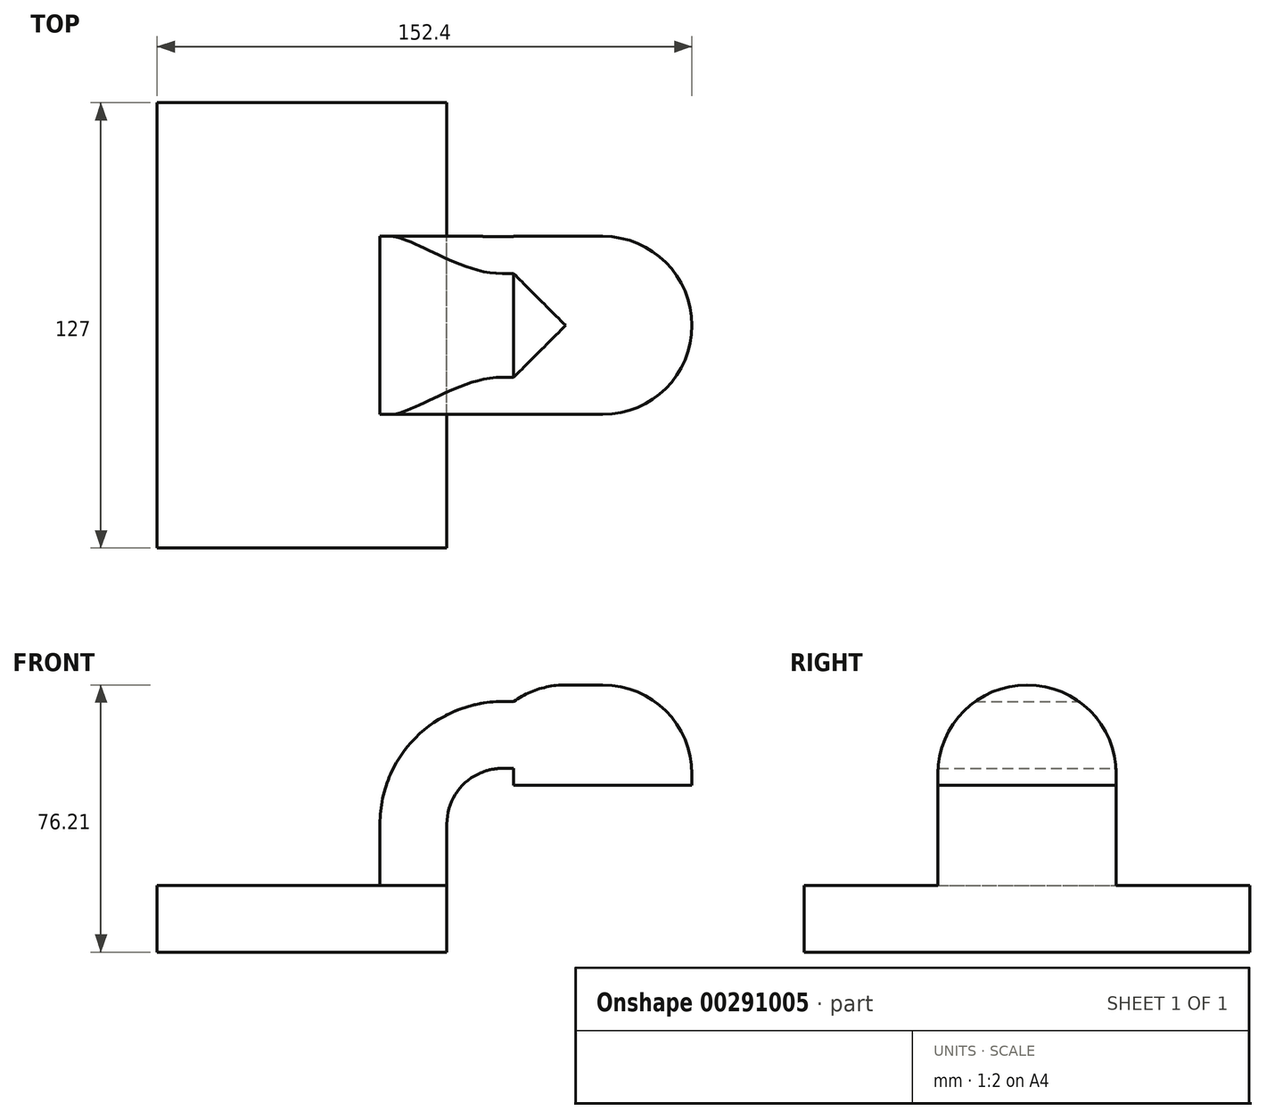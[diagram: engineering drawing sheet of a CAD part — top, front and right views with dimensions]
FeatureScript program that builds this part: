
annotation { "Feature Type Name" : "Feature", "Feature Type Description" : "" }
export const myFeature = defineFeature(function(context is Context, id is Id, definition is map)
    precondition{}
    {
        {
            var Q0;
            Q0=qCreatedBy(makeId("Front.planeOp"),FACE);
            var sketch = newSketch(context, id + "F0", { "sketchPlane" : qUnion([Q0])});
            skLineSegment(sketch, "E0.bottom", {"start": v(-41.28, 9.53) * mm, "end": v(41.28, 9.53) * mm});
            skLineSegment(sketch, "E0.top", {"start": v(-41.28, -9.52) * mm, "end": v(41.27, -9.52) * mm});
            skLineSegment(sketch, "E0.left", {"start": v(-41.28, 9.53) * mm, "end": v(-41.28, -9.52) * mm});
            skLineSegment(sketch, "E0.right", {"start": v(41.28, 9.53) * mm, "end": v(41.27, -9.52) * mm});
            skPoint(sketch, "E0.middle", {"position": v(0, 0) * mm});
            skLineSegment(sketch, "E1.bottom", {"start": v(111.13, 38.1) * mm, "end": v(60.33, 38.1) * mm});
            skLineSegment(sketch, "E1.top", {"start": v(111.13, 66.68) * mm, "end": v(60.33, 66.68) * mm});
            skLineSegment(sketch, "E1.left", {"start": v(111.13, 38.1) * mm, "end": v(111.13, 66.67) * mm});
            skLineSegment(sketch, "E1.right", {"start": v(60.33, 38.1) * mm, "end": v(60.33, 66.67) * mm});
            skPoint(sketch, "E1.middle", {"position": v(85.73, 52.39) * mm});
            skLineSegment(sketch, "E2", {"start": v(41.28, 9.53) * mm, "end": v(41.28, 27) * mm});
            skArc(sketch, "E3", {"start": v(41.27, 27) * mm, "mid": v(45.92, 38.23) * mm, "end": v(57.15, 42.88) * mm});
            skLineSegment(sketch, "E4", {"start": v(57.15, 42.88) * mm, "end": v(85.72, 42.88) * mm});
            skLineSegment(sketch, "E5.0", {"start": v(57.15, 61.93) * mm, "end": v(85.72, 61.93) * mm});
            skArc(sketch, "E5.1", {"start": v(22.22, 27) * mm, "mid": v(32.45, 51.7) * mm, "end": v(57.15, 61.93) * mm});
            skLineSegment(sketch, "E5.2", {"start": v(22.22, 9.53) * mm, "end": v(22.22, 27) * mm});
            skLineSegment(sketch, "E6", {"start": v(85.73, 38.1) * mm, "end": v(85.73, 66.68) * mm});
            skFitSpline(sketch, "E7", {"points": [v(-41.28, 9.53) * mm, v(57.15, 61.93) * mm], "startDerivative": vector(0.66, 117.01) * mm, "endDerivative": vector(162.8, -9.32) * mm});
            skSolve(sketch);
        }
        {
            var Q0;
            Q0=makeQuery(id+"F0.imprint","IMPRINT",FACE,{"disambiguationData":[TD([[makeQuery(id+"F0.imprint","IMPRINT",EDGE,{"derivedFrom":sQuery(id+"F0.wireOp",EDGE,"E0.top")}),1.0]])]});
            extrude(context, id + "F1", {"entities" : qUnion([Q0]), "endBound" : BoundingType.SYMMETRIC, "depth" : 127 * mm});
        }
        {
            var Q0;
            {var subQ1=sQuery(id+"F0.wireOp",EDGE,"E2");Q0=makeQuery(id+"F0.imprint","IMPRINT",FACE,{"disambiguationData":[TD([[makeQuery(id+"F0.imprint","IMPRINT",EDGE,{"derivedFrom":subQ1}),1.0]])]});}
            var Q1;
            {var subQ0=sQuery(id+"F0.wireOp",EDGE,"E4");var subQ1=sQuery(id+"F0.wireOp",EDGE,"E1.right");var subQ2=makeQuery(id+"F0.imprint","INTERSECT",VERTEX,{"derivedFrom":[subQ1,subQ0]});Q1=makeQuery(id+"F0.imprint","IMPRINT",FACE,{"disambiguationData":[TD([[makeQuery(id+"F0.imprint","IMPRINT",EDGE,{"disambiguationData":[TD([[subQ2,-1.0]])],"derivedFrom":subQ1}),-1.0]])]});}
            var Q2;
            {var subQ0=sQuery(id+"F0.wireOp",EDGE,"E1.right");var subQ1=sQuery(id+"F0.wireOp",EDGE,"E1.top");var subQ2=makeQuery(id+"F0.imprint","INTERSECT",VERTEX,{"derivedFrom":[subQ1,subQ0]});Q2=makeQuery(id+"F0.imprint","IMPRINT",FACE,{"disambiguationData":[TD([[makeQuery(id+"F0.imprint","IMPRINT",EDGE,{"disambiguationData":[TD([[subQ2,1.0]])],"derivedFrom":subQ1}),1.0]])]});}
            var Q3;
            {var subQ0=sQuery(id+"F0.wireOp",EDGE,"E1.right");var subQ1=sQuery(id+"F0.wireOp",EDGE,"E1.bottom");var subQ2=makeQuery(id+"F0.imprint","INTERSECT",VERTEX,{"derivedFrom":[subQ1,subQ0]});Q3=makeQuery(id+"F0.imprint","IMPRINT",FACE,{"disambiguationData":[TD([[makeQuery(id+"F0.imprint","IMPRINT",EDGE,{"disambiguationData":[TD([[subQ2,1.0]])],"derivedFrom":subQ1}),-1.0]])]});}
            extrude(context, id + "F2", {"entities" : qUnion([Q0, Q1, Q2, Q3]), "operationType" : NewBodyOperationType.ADD, "endBound" : BoundingType.SYMMETRIC, "depth" : 50.8 * mm});
        }
        {
            var Q0;
            Q0=makeQuery(id+"F0.imprint","IMPRINT",FACE,{"disambiguationData":[TD([[makeQuery(id+"F0.imprint","IMPRINT",EDGE,{"derivedFrom":sQuery(id+"F0.wireOp",EDGE,"E5.1")}),1.0]])]});
            extrude(context, id + "F3", {"entities" : qUnion([Q0]), "operationType" : NewBodyOperationType.ADD, "endBound" : BoundingType.SYMMETRIC, "depth" : 15.77 * mm});
        }
        {
            var Q0;
            {var subQ4=sQuery(id+"F0.wireOp",EDGE,"E1.left");Q0=makeQuery(id+"F0.imprint","IMPRINT",FACE,{"disambiguationData":[TD([[makeQuery(id+"F0.imprint","IMPRINT",EDGE,{"derivedFrom":subQ4}),1.0]])]});}
            var Q1;
            Q1=sQuery(id+"F0.wireOp",EDGE,"E6");
            revolve(context, id + "F4", {"operationType" : NewBodyOperationType.ADD, "entities" : qUnion([Q0]), "axis" : qUnion([Q1]), "revolveType" : RevolveType.FULL});
        }
        {
            var Q0;
            {var subQ0=sQuery(id+"F0.wireOp",EDGE,"E1.top");Q0=makeQuery(id+"F4.boolean.opBoolean","MERGE",FACE,{"derivedFrom":[makeQuery(id+"F2.opExtrude","SWEPT_FACE",FACE,{"disambiguationData":[OSD([subQ0])]}),makeQuery(id+"F4.opRevolve","SWEPT_FACE",FACE,{"disambiguationData":[OSD([subQ0])]})]});}
            fillet(context, id + "F5", {"entities" : qUnion([Q0]), "radius" : 25.4 * mm, "tangentPropagation" : true, "allowEdgeOverflow" : false});
        }
    });
